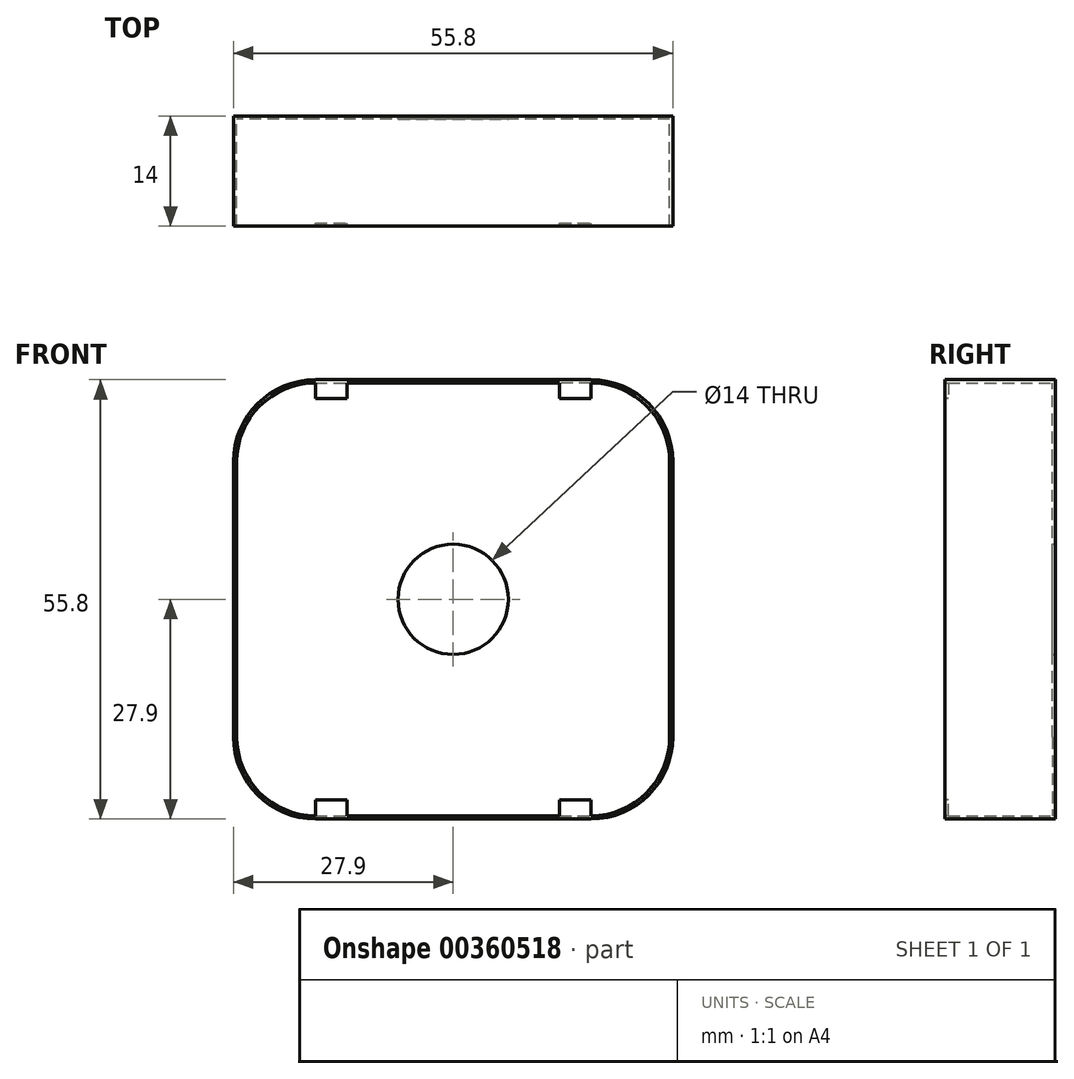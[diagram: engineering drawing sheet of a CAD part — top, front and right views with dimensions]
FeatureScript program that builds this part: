
annotation { "Feature Type Name" : "Feature", "Feature Type Description" : "" }
export const myFeature = defineFeature(function(context is Context, id is Id, definition is map)
    precondition{}
    {
        {
            var Q0;
            Q0=qCreatedBy(makeId("Front.planeOp"),FACE);
            var sketch = newSketch(context, id + "F0", { "sketchPlane" : qUnion([Q0])});
            skLineSegment(sketch, "E0.bottom", {"start": v(17.5, -27.5) * mm, "end": v(-17.5, -27.5) * mm});
            skLineSegment(sketch, "E0.top", {"start": v(17.5, 27.5) * mm, "end": v(-17.5, 27.5) * mm});
            skLineSegment(sketch, "E0.left", {"start": v(27.5, -17.5) * mm, "end": v(27.5, 17.5) * mm});
            skLineSegment(sketch, "E0.right", {"start": v(-27.5, -17.5) * mm, "end": v(-27.5, 17.5) * mm});
            skPoint(sketch, "E0.middle", {"position": v(0, 0) * mm});
            skPoint(sketch, "E1.visualSharp", {"position": v(-27.5, 27.5) * mm});
            skArc(sketch, "E1.filletArc", {"start": v(-17.5, 27.5) * mm, "mid": v(-24.57, 24.57) * mm, "end": v(-27.5, 17.5) * mm});
            skPoint(sketch, "E2.visualSharp", {"position": v(27.5, 27.5) * mm});
            skArc(sketch, "E2.filletArc", {"start": v(27.5, 17.5) * mm, "mid": v(24.57, 24.57) * mm, "end": v(17.5, 27.5) * mm});
            skPoint(sketch, "E3.visualSharp", {"position": v(27.5, -27.5) * mm});
            skArc(sketch, "E3.filletArc", {"start": v(17.5, -27.5) * mm, "mid": v(24.57, -24.57) * mm, "end": v(27.5, -17.5) * mm});
            skPoint(sketch, "E4.visualSharp", {"position": v(-27.5, -27.5) * mm});
            skArc(sketch, "E4.filletArc", {"start": v(-27.5, -17.5) * mm, "mid": v(-24.57, -24.57) * mm, "end": v(-17.5, -27.5) * mm});
            skCircle(sketch, "E5", {"center": v(0, 0) * mm, "radius": 7 * mm});
            skSolve(sketch);
        }
        {
            var Q0;
            Q0=makeQuery(id+"F0.imprint","IMPRINT",FACE,{"disambiguationData":[TD([[makeQuery(id+"F0.imprint","IMPRINT",EDGE,{"derivedFrom":sQuery(id+"F0.wireOp",EDGE,"E0.bottom")}),-1.0]])]});
            extrude(context, id + "F1", {"entities" : qUnion([Q0]), "depth" : .4 * mm});
        }
        {
            var Q0;
            Q0=qCreatedBy(makeId("Front.planeOp"),FACE);
            var sketch = newSketch(context, id + "F2", { "sketchPlane" : qUnion([Q0])});
            skLineSegment(sketch, "E6.bottom", {"start": v(17.5, -27.5) * mm, "end": v(-17.5, -27.5) * mm});
            skLineSegment(sketch, "E6.top", {"start": v(17.5, 27.5) * mm, "end": v(-17.5, 27.5) * mm});
            skLineSegment(sketch, "E6.left", {"start": v(27.5, -17.5) * mm, "end": v(27.5, 17.5) * mm});
            skLineSegment(sketch, "E6.right", {"start": v(-27.5, -17.5) * mm, "end": v(-27.5, 17.5) * mm});
            skPoint(sketch, "E6.middle", {"position": v(0, 0) * mm});
            skPoint(sketch, "E7.visualSharp", {"position": v(-27.5, 27.5) * mm});
            skArc(sketch, "E7.filletArc", {"start": v(-17.5, 27.5) * mm, "mid": v(-24.57, 24.57) * mm, "end": v(-27.5, 17.5) * mm});
            skPoint(sketch, "E8.visualSharp", {"position": v(27.5, 27.5) * mm});
            skArc(sketch, "E8.filletArc", {"start": v(27.5, 17.5) * mm, "mid": v(24.57, 24.57) * mm, "end": v(17.5, 27.5) * mm});
            skPoint(sketch, "E9.visualSharp", {"position": v(27.5, -27.5) * mm});
            skArc(sketch, "E9.filletArc", {"start": v(17.5, -27.5) * mm, "mid": v(24.57, -24.57) * mm, "end": v(27.5, -17.5) * mm});
            skPoint(sketch, "E10.visualSharp", {"position": v(-27.5, -27.5) * mm});
            skArc(sketch, "E10.filletArc", {"start": v(-27.5, -17.5) * mm, "mid": v(-24.57, -24.57) * mm, "end": v(-17.5, -27.5) * mm});
            skLineSegment(sketch, "E11.0", {"start": v(17.5, 27.9) * mm, "end": v(-17.5, 27.9) * mm});
            skArc(sketch, "E11.1", {"start": v(27.9, 17.5) * mm, "mid": v(24.85, 24.85) * mm, "end": v(17.5, 27.9) * mm});
            skArc(sketch, "E11.2", {"start": v(-17.5, 27.9) * mm, "mid": v(-24.85, 24.85) * mm, "end": v(-27.9, 17.5) * mm});
            skLineSegment(sketch, "E11.3", {"start": v(27.9, -17.5) * mm, "end": v(27.9, 17.5) * mm});
            skLineSegment(sketch, "E11.4", {"start": v(-27.9, -17.5) * mm, "end": v(-27.9, 17.5) * mm});
            skArc(sketch, "E11.5", {"start": v(-27.9, -17.5) * mm, "mid": v(-24.85, -24.85) * mm, "end": v(-17.5, -27.9) * mm});
            skLineSegment(sketch, "E11.6", {"start": v(17.5, -27.9) * mm, "end": v(-17.5, -27.9) * mm});
            skArc(sketch, "E11.7", {"start": v(17.5, -27.9) * mm, "mid": v(24.85, -24.85) * mm, "end": v(27.9, -17.5) * mm});
            skSolve(sketch);
        }
        {
            var Q0;
            Q0 = qSketchRegion(id + "F2", true);
            extrude(context, id + "F3", {"entities" : qUnion([Q0]), "operationType" : NewBodyOperationType.ADD, "depth" : 14 * mm});
        }
        {
            var Q0;
            Q0=makeQuery(id+"F3.opExtrude","CAP_EDGE",EDGE,{"disambiguationData":[OSD([sQuery(id+"F2.wireOp",EDGE,"E11.6")])],"isStart":false});
            var Q1;
            Q1=makeQuery(id+"F3.opExtrude","CAP_EDGE",EDGE,{"disambiguationData":[OSD([sQuery(id+"F2.wireOp",EDGE,"E11.0")])],"isStart":false});
            cPlane(context, id + "F4", {"entities" : qUnion([Q0, Q1]), "cplaneType" : CPlaneType.LINE_ANGLE, "offset" : 25 * mm, "angle" : 0 * degree, "width" : 150 * mm, "height" : 150 * mm});
        }
        {
            var Q0;
            Q0=qCreatedBy(id+"F4.planeOp",FACE);
            var sketch = newSketch(context, id + "F5", { "sketchPlane" : qUnion([Q0])});
            skPoint(sketch, "E12", {"position": v(-17.5, -27.9) * mm});
            skLineSegment(sketch, "E13.bottom", {"start": v(-17.5, -27.9) * mm, "end": v(-13.5, -27.9) * mm});
            skLineSegment(sketch, "E13.top", {"start": v(-17.5, -25.5) * mm, "end": v(-13.5, -25.5) * mm});
            skLineSegment(sketch, "E13.left", {"start": v(-17.5, -27.9) * mm, "end": v(-17.5, -25.5) * mm});
            skLineSegment(sketch, "E13.right", {"start": v(-13.5, -27.9) * mm, "end": v(-13.5, -25.5) * mm});
            skPoint(sketch, "E14", {"position": v(17.5, -27.9) * mm});
            skLineSegment(sketch, "E15.bottom", {"start": v(17.5, -27.9) * mm, "end": v(13.5, -27.9) * mm});
            skLineSegment(sketch, "E15.top", {"start": v(17.5, -25.5) * mm, "end": v(13.5, -25.5) * mm});
            skLineSegment(sketch, "E15.left", {"start": v(17.5, -27.9) * mm, "end": v(17.5, -25.5) * mm});
            skLineSegment(sketch, "E15.right", {"start": v(13.5, -27.9) * mm, "end": v(13.5, -25.5) * mm});
            skLineSegment(sketch, "E16.MirrorCS", {"start": v(17.5, 27.9) * mm, "end": v(17.5, 25.5) * mm});
            skLineSegment(sketch, "E17.MirrorCS", {"start": v(13.5, 27.9) * mm, "end": v(13.5, 25.5) * mm});
            skLineSegment(sketch, "E18.MirrorCS", {"start": v(-13.5, 27.9) * mm, "end": v(-13.5, 25.5) * mm});
            skLineSegment(sketch, "E19.MirrorCS", {"start": v(-17.5, 27.9) * mm, "end": v(-17.5, 25.5) * mm});
            skLineSegment(sketch, "E20.MirrorCS", {"start": v(17.5, 27.9) * mm, "end": v(13.5, 27.9) * mm});
            skLineSegment(sketch, "E21.MirrorCS", {"start": v(-17.5, 27.9) * mm, "end": v(-13.5, 27.9) * mm});
            skLineSegment(sketch, "E22.MirrorCS", {"start": v(-17.5, 25.5) * mm, "end": v(-13.5, 25.5) * mm});
            skLineSegment(sketch, "E23.MirrorCS", {"start": v(17.5, 25.5) * mm, "end": v(13.5, 25.5) * mm});
            skPoint(sketch, "E24.MirrorP", {"position": v(-17.5, 27.9) * mm});
            skPoint(sketch, "E25.MirrorP", {"position": v(17.5, 27.9) * mm});
            skSolve(sketch);
        }
        {
            var Q0;
            Q0 = qSketchRegion(id + "F5", true);
            extrude(context, id + "F6", {"entities" : qUnion([Q0]), "operationType" : NewBodyOperationType.ADD, "depth" : .4 * mm});
        }
    });
